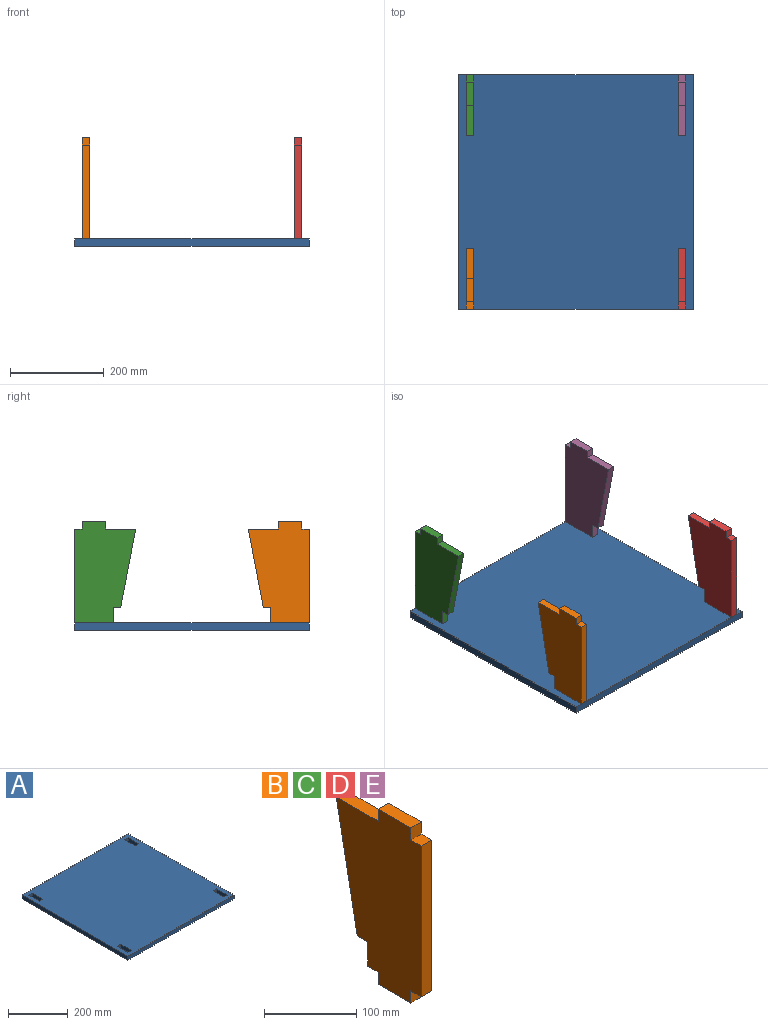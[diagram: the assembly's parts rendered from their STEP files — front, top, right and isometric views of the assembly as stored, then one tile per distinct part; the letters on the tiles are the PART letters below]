
ASSEMBLY  parts=5 mates=1
PART A: 22 faces, bbox 500x500x16 mm
  f0: plane 500x16mm, normal (1,0,0), area 8000mm2, adj f1,f3,f4,f5
  f1: plane 500x16mm, normal (0,1,0), area 8000mm2, adj f0,f2,f4,f5
  f2: plane 500x16mm, normal (-1,0,0), area 8000mm2, adj f1,f3,f4,f5
  f3: plane 500x16mm, normal (0,-1,0), area 8000mm2, adj f0,f2,f4,f5
  f4: plane 500x500mm, normal (0,0,1), area 246800mm2, adj f0,f1,f2,f3,f6,f7,f8,f9
  f5: plane 500x500mm, normal (0,0,-1), area 246800mm2, adj f0,f1,f2,f3,f6,f7,f8,f9
  f6: plane 16x16mm, normal (0,1,0), area 256mm2, adj f4,f5,f7,f8
  f7: plane 50x16mm, normal (1,0,0), area 800mm2, adj f4,f5,f6,f9
  f8: plane 50x16mm, normal (-1,0,0), area 800mm2, adj f4,f5,f6,f9
  f9: plane 16x16mm, normal (0,-1,0), area 256mm2, adj f4,f5,f7,f8
  f10: plane 16x16mm, normal (0,-1,0), area 256mm2, adj f4,f5,f11,f12
  f11: plane 50x16mm, normal (-1,0,0), area 800mm2, adj f4,f5,f10,f13
  f12: plane 50x16mm, normal (1,0,0), area 800mm2, adj f4,f5,f10,f13
  f13: plane 16x16mm, normal (0,1,0), area 256mm2, adj f4,f5,f11,f12
  f14: plane 16x16mm, normal (0,1,0), area 256mm2, adj f4,f5,f15,f16
  f15: plane 50x16mm, normal (1,0,0), area 800mm2, adj f4,f5,f14,f17
  f16: plane 50x16mm, normal (-1,0,0), area 800mm2, adj f4,f5,f14,f17
  f17: plane 16x16mm, normal (0,-1,0), area 256mm2, adj f4,f5,f15,f16
  f18: plane 16x16mm, normal (0,-1,0), area 256mm2, adj f4,f5,f19,f20
  f19: plane 50x16mm, normal (-1,0,0), area 800mm2, adj f4,f5,f18,f21
  f20: plane 50x16mm, normal (1,0,0), area 800mm2, adj f4,f5,f18,f21
  f21: plane 16x16mm, normal (0,1,0), area 256mm2, adj f4,f5,f19,f20
PART B: 16 faces, bbox 16x130x232 mm
  f0: plane 32x16mm, normal (0,1,0), area 512mm2, adj f4,f5,f12,f14
  f1: plane 200x16mm, normal (0,-1,0), area 3200mm2, adj f4,f5,f6,f11
  f2: plane 50x16mm, normal (0,0,-1), area 800mm2, adj f4,f5,f7,f13
  f3: plane 50x16mm, normal (0,0,1), area 800mm2, adj f4,f5,f9,f10
  f4: plane 232x130mm, normal (1,0,0), area 23376mm2, adj f0,f1,f2,f3,f6,f7,f8,f9
  f5: plane 232x130mm, normal (-1,0,0), area 23376mm2, adj f0,f1,f2,f3,f6,f7,f8,f9
  f6: plane 16x16mm, normal (0,0,-1), area 256mm2, adj f1,f4,f5,f7
  f7: plane 16x16mm, normal (0,-1,0), area 256mm2, adj f2,f4,f5,f6
  f8: plane 64x16mm, normal (0,0,1), area 1024mm2, adj f4,f5,f9,f15
  f9: plane 16x16mm, normal (0,1,0), area 256mm2, adj f3,f4,f5,f8
  f10: plane 16x16mm, normal (0,-1,0), area 256mm2, adj f3,f4,f5,f11
  f11: plane 16x16mm, normal (0,0,1), area 256mm2, adj f1,f4,f5,f10
  f12: plane 16x16mm, normal (0,0,-1), area 256mm2, adj f0,f4,f5,f13
  f13: plane 16x16mm, normal (0,1,0), area 256mm2, adj f2,f4,f5,f12
  f14: plane 16x16mm, normal (0,0,-1), area 256mm2, adj f0,f4,f5,f15
  f15: plane 168x32mm, normal (0,0.98,-0.19), area 2736.3mm2, adj f4,f5,f8,f14
PART C: same geometry as B
PART D: same geometry as B
PART E: same geometry as B
PLACE A t=(-250.14,298.31,-107.62)mm
PLACE B t=(-476.14,64.31,-107.62)mm
PLACE C rot(axis=(0,0,-1),180deg) t=(-476.14,532.31,-107.62)mm
PLACE D t=(-24.14,64.31,-107.62)mm
PLACE E rot(axis=(0,0,-1),180deg) t=(-24.14,532.31,-107.62)mm
MATE fastened A.f4 <-> B.f6  axis (0,0,1) through (-476.14,64.31,-91.62)mm
